# Revit family: RBA BIM - 8226
name_source: partatom
category: Specialty Equipment
revit_build: Autodesk Revit 2013 (Build: 20120221_2030)
units: mm (PartAtom-declared; Revit-internal decimal feet)

## types (3) — shared parameters
ADA Compliant = No
Assembly Code = C1030210
Bottle Diameter = 0.083
Bottle Material = Plastic Bobrick Soap Dispenser White
Bottle Radius = 0.041
Default Elevation = 1.219
Description = Lavatory-Mounted Soap Dispenser
Fixture Material = Stainless Steel Bobrick
Model = B-Series
Mounting Assembly Material = Plastic Bobrick Soap Dispenser Black
Neck Radius = 0.013
Top Assembly Height = 0.054

## per-type parameters (varying)
| type | Assembly Depth | Bottle Depth | Manufacturer | Maximum Mounting Depth | Mounting Depth | Mounting Depth Location | Spout Height | Spout Length | URL |
| B-822 | 0.371 | 0.243 | Bobrick Washroom Equipment, Inc. | 0.102 | 0.051 | 0.051 | 0.076 | 0.102 | www.bobrick.com |
| B-8221 | 0.21 | 0.156 | Bobrick Washroom Equipment, Inc. | 0.025 | 0.025 | 0.025 | 0.076 | 0.102 | www.bobrick.com |
| B-8226 | 0.371 | 0.243 | RBA Group | 0.102 | 0.051 | 0.051 | 0.098 | 0.152 | www.rba.com.au |

## geometry (parser evidence)
native form markers: Sweep x3
no freeform markers — native parametric forms only
